# Revit family: Assmbly_PC2-Pole_2Bkt-Opp_Rakks
name_source: partatom
category: Specialty Equipment
units: mm (PartAtom-declared; Revit-internal decimal feet)

## family parameters
Always vertical = Yes
Classification Number = 23.40.50.31.11.14
Cut with Voids When Loaded = No
Enable Cutting in Views = No
Maintain Annotation Orientation = No
Part Type = Normal
Room Calculation Point = No
Round Connector Dimension = Use Diameter
Shared = Yes
Work Plane-Based = No

## types (1)
- Assmbly_PC2-Pole_2Bkt-Opp_Rakks
    Assembly Code = E1010500
    Bracket Location = 0' - 0 3/8"
    Capacity (Weight) = 0.00 lb
    Construction Details = http://www.arcat.com
    Default Elevation = 0' - 0"
    Expected Lifespan (Years) = 0
    Green Building-LEED = http://www.arcat.com
    Installation-Fabrication = http://www.rakks.com
    Keynote = 10 56 00
    Maintenance Schedule (Months) = 0
    Manufacturer = Rangine Corp. - Rakks
    Manufacturer Fax = 781-455-8702
    Manufacturer Website = http://www.rakks.com
    Manufacturer's Notes = Aluminum Shelves may only be used with rectangular brackets
    Material = Metal - Clear Anodized
    Product Data = http://www.arcat.com
    Product Properties = http://www.arcat.com
    Revision = R1_03-2010
    Sales Information = http://store.rakks.com
    Send Message = http://www.arcat.com
    Shelf Overhang = 0' - 2"
    Specification = http://www.arcat.com
    Test Data = http://www.rakks.com
    Type Comments = Universal and Aria Brackets may not be used with SQ Standards
    URL = http://www.rakks.com
    Warranty Duration (Years) = 0

## geometry (parser evidence)
native form markers: Blend x20, Sweep x9
no freeform markers — native parametric forms only
